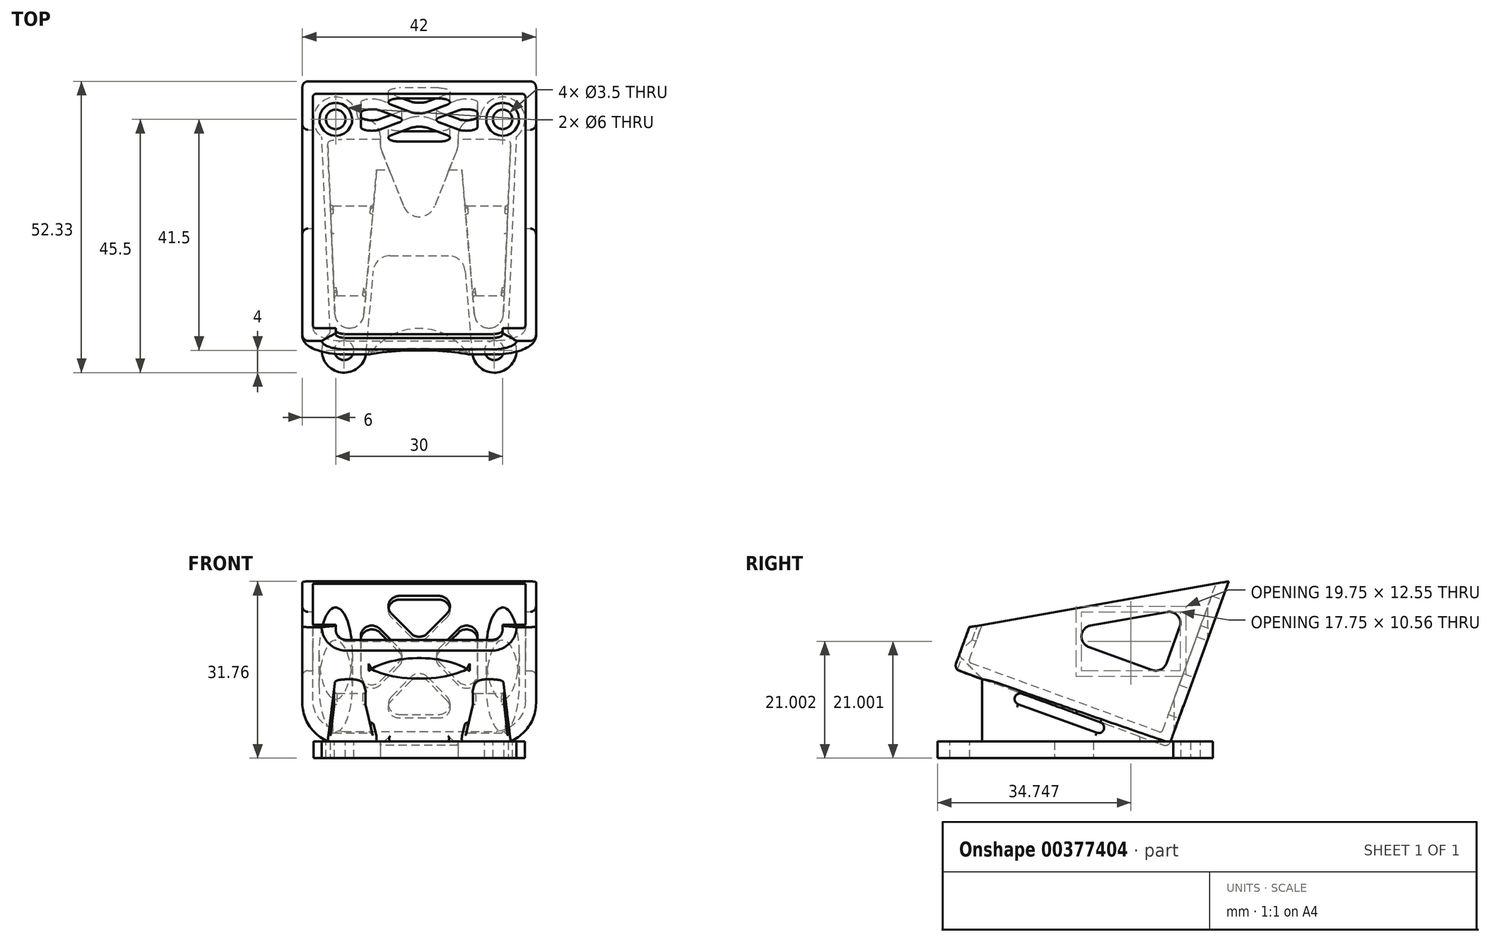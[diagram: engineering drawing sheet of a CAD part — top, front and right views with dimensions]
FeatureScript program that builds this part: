
annotation { "Feature Type Name" : "Feature", "Feature Type Description" : "" }
export const myFeature = defineFeature(function(context is Context, id is Id, definition is map)
    precondition{}
    {
        {
            var Q0;
            Q0=qCreatedBy(makeId("Right.planeOp"),FACE);
            var sketch = newSketch(context, id + "F0", { "sketchPlane" : qUnion([Q0])});
            skLineSegment(sketch, "E0.bottom", {"start": v(-38.53, 14.02) * mm, "end": v(0, 0) * mm});
            skLineSegment(sketch, "E0.top", {"start": v(-24.16, 53.49) * mm, "end": v(14.36, 39.47) * mm});
            skLineSegment(sketch, "E0.left", {"start": v(-38.53, 14.02) * mm, "end": v(-24.16, 53.49) * mm});
            skLineSegment(sketch, "E0.right", {"start": v(0, 0) * mm, "end": v(14.36, 39.47) * mm});
            skPoint(sketch, "E0.middle", {"position": v(-12.08, 26.74) * mm});
            skSolve(sketch);
        }
        {
            var Q0;
            Q0=makeQuery(id+"F0.imprint","IMPRINT",FACE,{"disambiguationData":[TD([[makeQuery(id+"F0.imprint","IMPRINT",EDGE,{"derivedFrom":sQuery(id+"F0.wireOp",EDGE,"E0.bottom")}),1.0]])]});
            extrude(context, id + "F1", {"entities" : qUnion([Q0]), "endBound" : BoundingType.SYMMETRIC, "depth" : 42 * mm});
        }
        {
            var Q0;
            Q0=qCreatedBy(makeId("Right.planeOp"),FACE);
            var sketch = newSketch(context, id + "F2", { "sketchPlane" : qUnion([Q0])});
            skLineSegment(sketch, "E1.bottom", {"start": v(-1.2, 2.56) * mm, "end": v(-35.96, 15.22) * mm});
            skLineSegment(sketch, "E1.top", {"start": v(11.8, 38.27) * mm, "end": v(-22.97, 50.93) * mm});
            skLineSegment(sketch, "E1.left", {"start": v(-1.2, 2.56) * mm, "end": v(11.8, 38.27) * mm});
            skLineSegment(sketch, "E1.right", {"start": v(-35.96, 15.22) * mm, "end": v(-22.97, 50.93) * mm});
            skPoint(sketch, "E1.middle", {"position": v(-12.08, 26.74) * mm});
            skSolve(sketch);
        }
        {
            var Q0;
            Q0=qSketchRegion(id+"F2",true);
            extrude(context, id + "F3", {"entities" : qUnion([Q0]), "operationType" : NewBodyOperationType.REMOVE, "endBound" : BoundingType.SYMMETRIC, "depth" : 38.2 * mm});
        }
        {
            var Q0;
            Q0=makeQuery(id+"F3.boolean.opBoolean","COPY",EDGE,{"derivedFrom":makeQuery(id+"F3.opExtrude","CAP_EDGE",EDGE,{"disambiguationData":[OSD([sQuery(id+"F2.wireOp",EDGE,"E1.top")])],"isStart":false})});
            var Q1;
            Q1=makeQuery(id+"F3.boolean.opBoolean","COPY",EDGE,{"derivedFrom":makeQuery(id+"F3.opExtrude","CAP_EDGE",EDGE,{"disambiguationData":[OSD([sQuery(id+"F2.wireOp",EDGE,"E1.bottom")])],"isStart":false})});
            var Q2;
            Q2=makeQuery(id+"F3.boolean.opBoolean","COPY",EDGE,{"derivedFrom":makeQuery(id+"F3.opExtrude","CAP_EDGE",EDGE,{"disambiguationData":[OSD([sQuery(id+"F2.wireOp",EDGE,"E1.bottom")])],"isStart":true})});
            var Q3;
            Q3=makeQuery(id+"F3.boolean.opBoolean","COPY",EDGE,{"derivedFrom":makeQuery(id+"F3.opExtrude","CAP_EDGE",EDGE,{"disambiguationData":[OSD([sQuery(id+"F2.wireOp",EDGE,"E1.top")])],"isStart":true})});
            fillet(context, id + "F4", {"entities" : qUnion([Q0, Q1, Q2, Q3]), "radius" : 6 * mm, "tangentPropagation" : true, "allowEdgeOverflow" : false});
        }
        {
            var Q0;
            Q0=makeQuery(id+"F1.opExtrude","CAP_EDGE",EDGE,{"disambiguationData":[OSD([sQuery(id+"F0.wireOp",EDGE,"E0.top")])],"isStart":false});
            var Q1;
            Q1=makeQuery(id+"F1.opExtrude","CAP_EDGE",EDGE,{"disambiguationData":[OSD([sQuery(id+"F0.wireOp",EDGE,"E0.top")])],"isStart":true});
            var Q2;
            Q2=makeQuery(id+"F1.opExtrude","CAP_EDGE",EDGE,{"disambiguationData":[OSD([sQuery(id+"F0.wireOp",EDGE,"E0.bottom")])],"isStart":true});
            var Q3;
            Q3=makeQuery(id+"F1.opExtrude","CAP_EDGE",EDGE,{"disambiguationData":[OSD([sQuery(id+"F0.wireOp",EDGE,"E0.bottom")])],"isStart":false});
            fillet(context, id + "F5", {"entities" : qUnion([Q0, Q1, Q2, Q3]), "radius" : 8 * mm, "tangentPropagation" : true, "allowEdgeOverflow" : false});
        }
        {
            var Q0;
            Q0=makeQuery(id+"F1.opExtrude","SWEPT_FACE",FACE,{"disambiguationData":[OSD([sQuery(id+"F0.wireOp",EDGE,"E0.left")])]});
            var sketch = newSketch(context, id + "F6", { "sketchPlane" : qUnion([Q0])});
            skLineSegment(sketch, "E2.bottom", {"start": v(-15, 36) * mm, "end": v(15, 36) * mm});
            skLineSegment(sketch, "E2.top", {"start": v(-15, 6) * mm, "end": v(15, 6) * mm});
            skLineSegment(sketch, "E2.left", {"start": v(-15, 36) * mm, "end": v(-15, 6) * mm});
            skLineSegment(sketch, "E2.right", {"start": v(15, 36) * mm, "end": v(15, 6) * mm});
            skSolve(sketch);
        }
        {
            var Q0;
            Q0=makeQuery(id+"F6.imprint","IMPRINT",FACE,{"disambiguationData":[TD([[makeQuery(id+"F6.imprint","IMPRINT",EDGE,{"derivedFrom":sQuery(id+"F6.wireOp",EDGE,"E2.bottom")}),-1.0]])]});
            extrude(context, id + "F7", {"entities" : qUnion([Q0]), "operationType" : NewBodyOperationType.REMOVE, "oppositeDirection" : true, "depth" : 25 * mm});
        }
        {
            var Q0;
            Q0=makeQuery(id+"F7.boolean.opBoolean","COPY",EDGE,{"derivedFrom":makeQuery(id+"F7.opExtrude","SWEPT_EDGE",EDGE,{"disambiguationData":[OSD([sQuery(id+"F6.wireOp",EDGE,"E2.top"),sQuery(id+"F6.wireOp",EDGE,"E2.left")])]})});
            var Q1;
            Q1=makeQuery(id+"F7.boolean.opBoolean","COPY",EDGE,{"derivedFrom":makeQuery(id+"F7.opExtrude","SWEPT_EDGE",EDGE,{"disambiguationData":[OSD([sQuery(id+"F6.wireOp",EDGE,"E2.top"),sQuery(id+"F6.wireOp",EDGE,"E2.right")])]})});
            var Q2;
            Q2=makeQuery(id+"F7.boolean.opBoolean","COPY",EDGE,{"derivedFrom":makeQuery(id+"F7.opExtrude","SWEPT_EDGE",EDGE,{"disambiguationData":[OSD([sQuery(id+"F6.wireOp",EDGE,"E2.bottom"),sQuery(id+"F6.wireOp",EDGE,"E2.right")])]})});
            var Q3;
            Q3=makeQuery(id+"F7.boolean.opBoolean","COPY",EDGE,{"derivedFrom":makeQuery(id+"F7.opExtrude","SWEPT_EDGE",EDGE,{"disambiguationData":[OSD([sQuery(id+"F6.wireOp",EDGE,"E2.bottom"),sQuery(id+"F6.wireOp",EDGE,"E2.left")])]})});
            fillet(context, id + "F8", {"entities" : qUnion([Q0, Q1, Q2, Q3]), "radius" : 2 * mm, "tangentPropagation" : true, "allowEdgeOverflow" : false});
        }
        {
            var Q0;
            Q0=qCreatedBy(makeId("Right.planeOp"),FACE);
            var sketch = newSketch(context, id + "F9", { "sketchPlane" : qUnion([Q0])});
            skLineSegment(sketch, "E3", {"start": v(-35.8, 21.54) * mm, "end": v(10.83, 29.76) * mm});
            skLineSegment(sketch, "E4", {"start": v(-35.8, 21.54) * mm, "end": v(-24.16, 53.49) * mm});
            skLineSegment(sketch, "E5", {"start": v(-24.16, 53.49) * mm, "end": v(14.36, 39.47) * mm});
            skLineSegment(sketch, "E6", {"start": v(14.36, 39.47) * mm, "end": v(10.83, 29.76) * mm});
            skSolve(sketch);
        }
        {
            var Q0;
            Q0=qSketchRegion(id+"F9",true);
            extrude(context, id + "F10", {"entities" : qUnion([Q0]), "operationType" : NewBodyOperationType.REMOVE, "endBound" : BoundingType.SYMMETRIC, "oppositeDirection" : true, "depth" : 50 * mm});
        }
        {
            var Q0;
            Q0=makeQuery(id+"F8.opFillet","BLEND_EDGE",EDGE,{"blendedFrom":[makeQuery(id+"F7.boolean.opBoolean","COPY",EDGE,{"derivedFrom":makeQuery(id+"F7.opExtrude","SWEPT_EDGE",EDGE,{"disambiguationData":[OSD([sQuery(id+"F6.wireOp",EDGE,"E2.top"),sQuery(id+"F6.wireOp",EDGE,"E2.left")])]})}),makeQuery(id+"F1.opExtrude","SWEPT_FACE",FACE,{"disambiguationData":[OSD([sQuery(id+"F0.wireOp",EDGE,"E0.left")])]})],"blendedInto":[makeQuery(id+"F1.opExtrude","SWEPT_FACE",FACE,{"disambiguationData":[OSD([sQuery(id+"F0.wireOp",EDGE,"E0.left")])]})]});
            chamfer(context, id + "F11", {"entities" : qUnion([Q0]), "chamferType" : ChamferType.TWO_OFFSETS, "width1" : 2.5 * mm, "oppositeDirection" : false, "width2" : 1.25 * mm, "tangentPropagation" : true});
        }
        {
            var Q0;
            Q0=makeQuery(id+"F1.opExtrude","CAP_EDGE",EDGE,{"disambiguationData":[OSD([sQuery(id+"F0.wireOp",EDGE,"E0.right")])],"isStart":false});
            var Q1;
            Q1=makeQuery(id+"F5.opFillet","BLEND_EDGE",EDGE,{"blendedFrom":[makeQuery(id+"F1.opExtrude","CAP_EDGE",EDGE,{"disambiguationData":[OSD([sQuery(id+"F0.wireOp",EDGE,"E0.bottom")])],"isStart":false}),makeQuery(id+"F1.opExtrude","SWEPT_FACE",FACE,{"disambiguationData":[OSD([sQuery(id+"F0.wireOp",EDGE,"E0.left")])]})],"blendedInto":[makeQuery(id+"F1.opExtrude","SWEPT_FACE",FACE,{"disambiguationData":[OSD([sQuery(id+"F0.wireOp",EDGE,"E0.left")])]})]});
            fillet(context, id + "F12", {"entities" : qUnion([Q0, Q1]), "radius" : 1 * mm, "tangentPropagation" : true, "allowEdgeOverflow" : false});
        }
        {
            var Q0;
            Q0=qCreatedBy(makeId("Top.planeOp"),FACE);
            var sketch = newSketch(context, id + "F13", { "sketchPlane" : qUnion([Q0])});
            skCircle(sketch, "E7", {"center": v(-13.5, -37.5) * mm, "radius": 1.75 * mm, "construction": true});
            skCircle(sketch, "E8", {"center": v(-15, 4) * mm, "radius": 1.75 * mm, "construction": true});
            skCircle(sketch, "E9.MirrorC", {"center": v(15, 4) * mm, "radius": 1.75 * mm, "construction": true});
            skCircle(sketch, "E10.MirrorC", {"center": v(13.5, -37.5) * mm, "radius": 1.75 * mm, "construction": true});
            skArc(sketch, "E11", {"start": v(-16, -34.38) * mm, "mid": v(-15.39, -41.03) * mm, "end": v(-9.52, -37.85) * mm});
            skArc(sketch, "E12", {"start": v(9.52, -37.85) * mm, "mid": v(15.39, -41.03) * mm, "end": v(16, -34.38) * mm});
            skArc(sketch, "E13", {"start": v(-11, 4) * mm, "mid": v(-16.73, 7.6) * mm, "end": v(-17.5, 0.88) * mm});
            skArc(sketch, "E14", {"start": v(17.5, 0.88) * mm, "mid": v(16.73, 7.6) * mm, "end": v(11, 4) * mm});
            skLineSegment(sketch, "E15", {"start": v(-9.52, -37.85) * mm, "end": v(-8.24, -23.24) * mm});
            skLineSegment(sketch, "E16", {"start": v(-5.25, -20.5) * mm, "end": v(5.25, -20.5) * mm});
            skLineSegment(sketch, "E17", {"start": v(8.24, -23.24) * mm, "end": v(9.52, -37.85) * mm});
            skPoint(sketch, "E18.visualSharp", {"position": v(-8, -20.5) * mm});
            skArc(sketch, "E18.filletArc", {"start": v(-5.25, -20.5) * mm, "mid": v(-7.28, -21.29) * mm, "end": v(-8.24, -23.24) * mm});
            skPoint(sketch, "E19.visualSharp", {"position": v(8, -20.5) * mm});
            skArc(sketch, "E19.filletArc", {"start": v(8.24, -23.24) * mm, "mid": v(7.28, -21.29) * mm, "end": v(5.25, -20.5) * mm});
            skLineSegment(sketch, "E20", {"start": v(-16, -34.38) * mm, "end": v(-17.5, 0.88) * mm});
            skLineSegment(sketch, "E21.MirrorCS", {"start": v(16, -34.38) * mm, "end": v(17.5, 0.88) * mm});
            skLineSegment(sketch, "E22", {"start": v(-11, 4) * mm, "end": v(-7, 4) * mm});
            skLineSegment(sketch, "E23", {"start": v(-7, 4) * mm, "end": v(-7, -0.43) * mm});
            skLineSegment(sketch, "E24", {"start": v(-6.79, -1.53) * mm, "end": v(-2.79, -11.6) * mm});
            skLineSegment(sketch, "E25.MirrorCS", {"start": v(7, 4) * mm, "end": v(7, -0.43) * mm});
            skLineSegment(sketch, "E26.MirrorCS", {"start": v(6.79, -1.53) * mm, "end": v(2.79, -11.6) * mm});
            skPoint(sketch, "E27.visualSharp", {"position": v(0, -18.63) * mm});
            skArc(sketch, "E27.filletArc", {"start": v(-2.79, -11.6) * mm, "mid": v(0, -13.5) * mm, "end": v(2.79, -11.6) * mm});
            skPoint(sketch, "E28.visualSharp", {"position": v(-7, -1) * mm});
            skArc(sketch, "E28.filletArc", {"start": v(-7, -0.43) * mm, "mid": v(-6.95, -0.99) * mm, "end": v(-6.79, -1.53) * mm});
            skPoint(sketch, "E29.visualSharp", {"position": v(7, -1) * mm});
            skArc(sketch, "E29.filletArc", {"start": v(6.79, -1.53) * mm, "mid": v(6.95, -0.99) * mm, "end": v(7, -0.43) * mm});
            skLineSegment(sketch, "E30.trimOffspring", {"start": v(7, 4) * mm, "end": v(11, 4) * mm});
            skSolve(sketch);
        }
        {
            var Q0;
            Q0=qSketchRegion(id+"F13",true);
            extrude(context, id + "F14", {"entities" : qUnion([Q0]), "operationType" : NewBodyOperationType.ADD, "depth" : 1 * mm, "hasSecondDirection" : true, "secondDirectionOppositeDirection" : true, "secondDirectionDepth" : 2 * mm});
        }
        {
            var Q0;
            {var subQ0=sQuery(id+"F13.wireOp",EDGE,"E16");var subQ2=sQuery(id+"F13.wireOp",EDGE,"E14");var subQ4=sQuery(id+"F13.wireOp",EDGE,"E12");var subQ5=makeQuery(id+"F14.opExtrude","SWEPT_FACE",FACE,{"disambiguationData":[OSD([subQ4])]});var subQ6=sQuery(id+"F0.wireOp",EDGE,"E0.bottom");var subQ9=sQuery(id+"F13.wireOp",EDGE,"E17");var subQ11=sQuery(id+"F13.wireOp",EDGE,"E19.filletArc");var subQ13=sQuery(id+"F13.wireOp",EDGE,"E21.MirrorCS");var subQ15=sQuery(id+"F13.wireOp",EDGE,"E15");var subQ16=sQuery(id+"F13.wireOp",EDGE,"E13");var subQ17=sQuery(id+"F13.wireOp",EDGE,"E11");var subQ18=sQuery(id+"F13.wireOp",EDGE,"E18.filletArc");var subQ19=sQuery(id+"F13.wireOp",EDGE,"E20");Q0=makeQuery(id+"FU2tXwDnlWeOjY7_1.boolean.opBoolean","SPLIT",FACE,{"disambiguationData":[TD([subQ5])],"derivedFrom":makeQuery(id+"F14.boolean.opBoolean","SPLIT",FACE,{"disambiguationData":[TD([makeQuery(id+"F1.opExtrude","SWEPT_FACE",FACE,{"disambiguationData":[OSD([subQ6])]})])],"derivedFrom":makeQuery(id+"F14.opExtrude","CAP_FACE",FACE,{"disambiguationData":[OSD([subQ17,subQ4,subQ16,subQ2,subQ15,subQ0,subQ9,subQ18,subQ11,subQ19,subQ13,sQuery(id+"F13.wireOp",EDGE,"LFwfzHnZ-pg1Y-ZXRW-QcZN-Bii3daT9BQZJ")])],"isStart":false})})});}
            var sketch = newSketch(context, id + "F15", { "sketchPlane" : qUnion([Q0])});
            skCircle(sketch, "E31", {"center": v(15, 4) * mm, "radius": 1.75 * mm});
            skCircle(sketch, "E32.MirrorC", {"center": v(-15, 4) * mm, "radius": 1.75 * mm});
            skSolve(sketch);
        }
        {
            var Q0;
            Q0=qSketchRegion(id+"F15",true);
            extrude(context, id + "F16", {"entities" : qUnion([Q0]), "operationType" : NewBodyOperationType.REMOVE, "depth" : 30 * mm});
        }
        {
            var Q0;
            Q0=qSketchRegion(id+"F15",true);
            extrude(context, id + "F17", {"entities" : qUnion([Q0]), "operationType" : NewBodyOperationType.REMOVE, "oppositeDirection" : true, "depth" : 1 * mm});
        }
        {
            var Q0;
            {var subQ0=sQuery(id+"F13.wireOp",EDGE,"E15");var subQ1=sQuery(id+"F13.wireOp",EDGE,"E13");var subQ2=sQuery(id+"F13.wireOp",EDGE,"E11");var subQ3=sQuery(id+"F13.wireOp",EDGE,"E20");var subQ6=sQuery(id+"F13.wireOp",EDGE,"E16");var subQ7=sQuery(id+"F13.wireOp",EDGE,"E18.filletArc");Q0=makeQuery(id+"F16.boolean.opBoolean","MERGE",FACE,{"derivedFrom":[makeQuery(id+"FU2tXwDnlWeOjY7_1.boolean.opBoolean","SPLIT",FACE,{"disambiguationData":[TD([makeQuery(id+"F14.opExtrude","SWEPT_FACE",FACE,{"disambiguationData":[OSD([subQ2])]})])],"derivedFrom":makeQuery(id+"F14.opExtrude","CAP_FACE",FACE,{"disambiguationData":[OSD([subQ2,sQuery(id+"F13.wireOp",EDGE,"E12"),subQ1,sQuery(id+"F13.wireOp",EDGE,"E14"),subQ0,subQ6,sQuery(id+"F13.wireOp",EDGE,"E17"),subQ7,sQuery(id+"F13.wireOp",EDGE,"E19.filletArc"),subQ3,sQuery(id+"F13.wireOp",EDGE,"E21.MirrorCS"),sQuery(id+"F13.wireOp",EDGE,"LFwfzHnZ-pg1Y-ZXRW-QcZN-Bii3daT9BQZJ")])],"isStart":false})}),makeQuery(id+"F16.opExtrude","CAP_FACE",FACE,{"disambiguationData":[OSD([sQuery(id+"F15.wireOp",EDGE,"E32.MirrorC")])],"isStart":true})]});}
            var sketch = newSketch(context, id + "F18", { "sketchPlane" : qUnion([Q0])});
            skCircle(sketch, "E33", {"center": v(-13.5, -37.5) * mm, "radius": 1.75 * mm});
            skCircle(sketch, "E34", {"center": v(-15, 4) * mm, "radius": 1.75 * mm});
            skCircle(sketch, "E35.MirrorC", {"center": v(13.5, -37.5) * mm, "radius": 1.75 * mm});
            skCircle(sketch, "E36.MirrorC", {"center": v(15, 4) * mm, "radius": 1.75 * mm});
            skSolve(sketch);
        }
        {
            var Q0;
            Q0=qSketchRegion(id+"F18",true);
            extrude(context, id + "F19", {"entities" : qUnion([Q0]), "operationType" : NewBodyOperationType.REMOVE, "oppositeDirection" : true, "depth" : 25 * mm});
        }
        {
            var Q0;
            Q0=makeQuery(id+"F14.opExtrude","CAP_FACE",FACE,{"disambiguationData":[OSD([sQuery(id+"F13.wireOp",EDGE,"E11"),sQuery(id+"F13.wireOp",EDGE,"E12"),sQuery(id+"F13.wireOp",EDGE,"E13"),sQuery(id+"F13.wireOp",EDGE,"E14"),sQuery(id+"F13.wireOp",EDGE,"E15"),sQuery(id+"F13.wireOp",EDGE,"E16"),sQuery(id+"F13.wireOp",EDGE,"E17"),sQuery(id+"F13.wireOp",EDGE,"E18.filletArc"),sQuery(id+"F13.wireOp",EDGE,"E19.filletArc"),sQuery(id+"F13.wireOp",EDGE,"E20"),sQuery(id+"F13.wireOp",EDGE,"E21.MirrorCS"),sQuery(id+"F13.wireOp",EDGE,"E22"),sQuery(id+"F13.wireOp",EDGE,"E23"),sQuery(id+"F13.wireOp",EDGE,"E24"),sQuery(id+"F13.wireOp",EDGE,"E25.MirrorCS"),sQuery(id+"F13.wireOp",EDGE,"E26.MirrorCS"),sQuery(id+"F13.wireOp",EDGE,"E27.filletArc"),sQuery(id+"F13.wireOp",EDGE,"E28.filletArc"),sQuery(id+"F13.wireOp",EDGE,"E29.filletArc"),sQuery(id+"F13.wireOp",EDGE,"E30.trimOffspring")])],"isStart":false});
            var sketch = newSketch(context, id + "F20", { "sketchPlane" : qUnion([Q0])});
            skLineSegment(sketch, "E37", {"start": v(-15.04, -33.5) * mm, "end": v(-16.44, -0.47) * mm});
            skLineSegment(sketch, "E38", {"start": v(-10.14, -33.5) * mm, "end": v(-7.45, -2.75) * mm});
            skLineSegment(sketch, "E39", {"start": v(-16.44, -0.47) * mm, "end": v(-7.45, -0.47) * mm});
            skLineSegment(sketch, "E40", {"start": v(-7.45, -0.47) * mm, "end": v(-7.45, -2.75) * mm});
            skLineSegment(sketch, "E41.MirrorCS", {"start": v(7.45, -0.47) * mm, "end": v(7.45, -2.75) * mm});
            skLineSegment(sketch, "E42.MirrorCS", {"start": v(10.14, -33.5) * mm, "end": v(7.45, -2.75) * mm});
            skLineSegment(sketch, "E43.MirrorCS", {"start": v(15.04, -33.5) * mm, "end": v(16.44, -0.47) * mm});
            skLineSegment(sketch, "E44.MirrorCS", {"start": v(16.44, -0.47) * mm, "end": v(7.45, -0.47) * mm});
            skPoint(sketch, "E45.orphan", {"position": v(-10.05, -32.46) * mm});
            skPoint(sketch, "E46.orphan", {"position": v(10.05, -32.46) * mm});
            skLineSegment(sketch, "E47", {"start": v(-15.04, -33.5) * mm, "end": v(-10.14, -33.5) * mm});
            skPoint(sketch, "E48.center.orphan", {"position": v(-13.5, -37.5) * mm});
            skLineSegment(sketch, "E49.MirrorCS", {"start": v(15.04, -33.5) * mm, "end": v(10.14, -33.5) * mm});
            skSolve(sketch);
        }
        {
            var Q0;
            Q0=qSketchRegion(id+"F20",true);
            extrude(context, id + "F21", {"entities" : qUnion([Q0]), "operationType" : NewBodyOperationType.ADD, "depth" : 17 * mm});
        }
        {
            var Q0;
            Q0=makeQuery(id+"F3.boolean.opBoolean","COPY",FACE,{"derivedFrom":makeQuery(id+"F3.opExtrude","SWEPT_FACE",FACE,{"disambiguationData":[OSD([sQuery(id+"F2.wireOp",EDGE,"E1.left")])]})});
            var sketch = newSketch(context, id + "F22", { "sketchPlane" : qUnion([Q0])});
            skLineSegment(sketch, "E50.bottom", {"start": v(-19.1, 28.52) * mm, "end": v(19.1, 28.52) * mm});
            skLineSegment(sketch, "E50.top", {"start": v(-13.1, 2) * mm, "end": v(13.1, 2) * mm});
            skLineSegment(sketch, "E50.left", {"start": v(-19.1, 28.52) * mm, "end": v(-19.1, 8) * mm});
            skLineSegment(sketch, "E50.right", {"start": v(19.1, 28.52) * mm, "end": v(19.1, 8) * mm});
            skPoint(sketch, "E51.visualSharp", {"position": v(-19.1, 2) * mm});
            skArc(sketch, "E51.filletArc", {"start": v(-19.1, 8) * mm, "mid": v(-17.34, 3.76) * mm, "end": v(-13.1, 2) * mm});
            skPoint(sketch, "E52.visualSharp", {"position": v(19.1, 2) * mm});
            skArc(sketch, "E52.filletArc", {"start": v(13.1, 2) * mm, "mid": v(17.34, 3.76) * mm, "end": v(19.1, 8) * mm});
            skSolve(sketch);
        }
        {
            var Q0;
            Q0=qSketchRegion(id+"F22",true);
            extrude(context, id + "F23", {"entities" : qUnion([Q0]), "operationType" : NewBodyOperationType.REMOVE, "depth" : 36 * mm});
        }
        {
            var Q0;
            Q0=makeQuery(id+"F14.opExtrude","SWEPT_EDGE",EDGE,{"disambiguationData":[OSD([sQuery(id+"F13.wireOp",EDGE,"E25.MirrorCS"),sQuery(id+"F13.wireOp",EDGE,"E30.trimOffspring")])]});
            var Q1;
            Q1=makeQuery(id+"F14.opExtrude","SWEPT_EDGE",EDGE,{"disambiguationData":[OSD([sQuery(id+"F13.wireOp",EDGE,"E22"),sQuery(id+"F13.wireOp",EDGE,"E23")])]});
            fillet(context, id + "F24", {"entities" : qUnion([Q0, Q1]), "radius" : 3 * mm, "tangentPropagation" : true, "allowEdgeOverflow" : false});
        }
        {
            var Q0;
            Q0=makeQuery(id+"F14.opExtrude","SWEPT_EDGE",EDGE,{"disambiguationData":[OSD([sQuery(id+"F13.wireOp",EDGE,"E13"),sQuery(id+"F13.wireOp",EDGE,"E22")])]});
            var Q1;
            Q1=makeQuery(id+"F14.opExtrude","SWEPT_EDGE",EDGE,{"disambiguationData":[OSD([sQuery(id+"F13.wireOp",EDGE,"E14"),sQuery(id+"F13.wireOp",EDGE,"E30.trimOffspring")])]});
            var Q2;
            Q2=makeQuery(id+"F14.opExtrude","SWEPT_EDGE",EDGE,{"disambiguationData":[OSD([sQuery(id+"F13.wireOp",EDGE,"E12"),sQuery(id+"F13.wireOp",EDGE,"E21.MirrorCS")])]});
            var Q3;
            Q3=makeQuery(id+"F14.opExtrude","SWEPT_EDGE",EDGE,{"disambiguationData":[OSD([sQuery(id+"F13.wireOp",EDGE,"E11"),sQuery(id+"F13.wireOp",EDGE,"E20")])]});
            fillet(context, id + "F25", {"entities" : qUnion([Q0, Q1, Q2, Q3]), "radius" : 0.5 * mm, "tangentPropagation" : true, "allowEdgeOverflow" : false});
        }
        {
            var Q0;
            Q0=makeQuery(id+"F14.boolean.opBoolean","INTERSECT",EDGE,{"disambiguationData":[OD(0.0)],"derivedFrom":[makeQuery(id+"F1.opExtrude","SWEPT_FACE",FACE,{"disambiguationData":[OSD([sQuery(id+"F0.wireOp",EDGE,"E0.bottom")])]}),makeQuery(id+"F14.opExtrude","CAP_FACE",FACE,{"disambiguationData":[OSD([sQuery(id+"F13.wireOp",EDGE,"E11"),sQuery(id+"F13.wireOp",EDGE,"E12"),sQuery(id+"F13.wireOp",EDGE,"E13"),sQuery(id+"F13.wireOp",EDGE,"E14"),sQuery(id+"F13.wireOp",EDGE,"E15"),sQuery(id+"F13.wireOp",EDGE,"E16"),sQuery(id+"F13.wireOp",EDGE,"E17"),sQuery(id+"F13.wireOp",EDGE,"E18.filletArc"),sQuery(id+"F13.wireOp",EDGE,"E19.filletArc"),sQuery(id+"F13.wireOp",EDGE,"E20"),sQuery(id+"F13.wireOp",EDGE,"E21.MirrorCS"),sQuery(id+"F13.wireOp",EDGE,"E22"),sQuery(id+"F13.wireOp",EDGE,"E23"),sQuery(id+"F13.wireOp",EDGE,"E24"),sQuery(id+"F13.wireOp",EDGE,"E25.MirrorCS"),sQuery(id+"F13.wireOp",EDGE,"E26.MirrorCS"),sQuery(id+"F13.wireOp",EDGE,"E27.filletArc"),sQuery(id+"F13.wireOp",EDGE,"E28.filletArc"),sQuery(id+"F13.wireOp",EDGE,"E29.filletArc"),sQuery(id+"F13.wireOp",EDGE,"E30.trimOffspring")])],"isStart":false})]});
            var Q1;
            Q1=makeQuery(id+"F14.boolean.opBoolean","INTERSECT",EDGE,{"disambiguationData":[OD(1.0)],"derivedFrom":[makeQuery(id+"F1.opExtrude","SWEPT_FACE",FACE,{"disambiguationData":[OSD([sQuery(id+"F0.wireOp",EDGE,"E0.bottom")])]}),makeQuery(id+"F14.opExtrude","CAP_FACE",FACE,{"disambiguationData":[OSD([sQuery(id+"F13.wireOp",EDGE,"E11"),sQuery(id+"F13.wireOp",EDGE,"E12"),sQuery(id+"F13.wireOp",EDGE,"E13"),sQuery(id+"F13.wireOp",EDGE,"E14"),sQuery(id+"F13.wireOp",EDGE,"E15"),sQuery(id+"F13.wireOp",EDGE,"E16"),sQuery(id+"F13.wireOp",EDGE,"E17"),sQuery(id+"F13.wireOp",EDGE,"E18.filletArc"),sQuery(id+"F13.wireOp",EDGE,"E19.filletArc"),sQuery(id+"F13.wireOp",EDGE,"E20"),sQuery(id+"F13.wireOp",EDGE,"E21.MirrorCS"),sQuery(id+"F13.wireOp",EDGE,"E22"),sQuery(id+"F13.wireOp",EDGE,"E23"),sQuery(id+"F13.wireOp",EDGE,"E24"),sQuery(id+"F13.wireOp",EDGE,"E25.MirrorCS"),sQuery(id+"F13.wireOp",EDGE,"E26.MirrorCS"),sQuery(id+"F13.wireOp",EDGE,"E27.filletArc"),sQuery(id+"F13.wireOp",EDGE,"E28.filletArc"),sQuery(id+"F13.wireOp",EDGE,"E29.filletArc"),sQuery(id+"F13.wireOp",EDGE,"E30.trimOffspring")])],"isStart":false})]});
            fillet(context, id + "F26", {"entities" : qUnion([Q0, Q1]), "radius" : 0.5 * mm, "tangentPropagation" : true, "allowEdgeOverflow" : false});
        }
        {
            var Q0;
            Q0=qCreatedBy(makeId("Right.planeOp"),FACE);
            var sketch = newSketch(context, id + "F27", { "sketchPlane" : qUnion([Q0])});
            skLineSegment(sketch, "E53", {"start": v(-13.98, 21.83) * mm, "end": v(-0.22, 24.26) * mm});
            skLineSegment(sketch, "E54", {"start": v(2.01, 21.6) * mm, "end": v(-0.38, 15.04) * mm});
            skLineSegment(sketch, "E55", {"start": v(-2.94, 13.84) * mm, "end": v(-14.32, 17.98) * mm});
            skPoint(sketch, "E56.visualSharp", {"position": v(-21.33, 20.54) * mm});
            skArc(sketch, "E56.filletArc", {"start": v(-13.98, 21.83) * mm, "mid": v(-15.63, 20.04) * mm, "end": v(-14.32, 17.98) * mm});
            skPoint(sketch, "E57.visualSharp", {"position": v(3.2, 24.86) * mm});
            skArc(sketch, "E57.filletArc", {"start": v(2.01, 21.6) * mm, "mid": v(1.66, 23.58) * mm, "end": v(-0.22, 24.26) * mm});
            skPoint(sketch, "E58.visualSharp", {"position": v(-1.06, 13.16) * mm});
            skArc(sketch, "E58.filletArc", {"start": v(-2.94, 13.84) * mm, "mid": v(-1.41, 13.9) * mm, "end": v(-0.38, 15.04) * mm});
            skSolve(sketch);
        }
        {
            var Q0;
            Q0=qSketchRegion(id+"F27",true);
            extrude(context, id + "F28", {"entities" : qUnion([Q0]), "operationType" : NewBodyOperationType.REMOVE, "endBound" : BoundingType.SYMMETRIC, "oppositeDirection" : true, "depth" : 50 * mm});
        }
        {
            var Q0;
            Q0=makeQuery(id+"F1.opExtrude","SWEPT_FACE",FACE,{"disambiguationData":[OSD([sQuery(id+"F0.wireOp",EDGE,"E0.right")])]});
            var sketch = newSketch(context, id + "F29", { "sketchPlane" : qUnion([Q0])});
            skLineSegment(sketch, "E59.bottom", {"start": v(-3.54, 28.17) * mm, "end": v(3.54, 28.17) * mm});
            skLineSegment(sketch, "E59.top", {"start": v(-3.54, 5.5) * mm, "end": v(3.54, 5.5) * mm});
            skLineSegment(sketch, "E59.left", {"start": v(-10.5, 20.5) * mm, "end": v(-10.5, 13.18) * mm});
            skLineSegment(sketch, "E59.right", {"start": v(10.5, 20.5) * mm, "end": v(10.5, 13.18) * mm});
            skLineSegment(sketch, "E60", {"start": v(-5, 24.81) * mm, "end": v(-1.47, 21) * mm});
            skLineSegment(sketch, "E61", {"start": v(-10.5, 28.17) * mm, "end": v(10.5, 5.5) * mm, "construction": true});
            skLineSegment(sketch, "E62", {"start": v(10.5, 28.17) * mm, "end": v(-10.5, 5.5) * mm, "construction": true});
            skLineSegment(sketch, "E63", {"start": v(-7.03, 21.85) * mm, "end": v(-3.64, 18.2) * mm});
            skLineSegment(sketch, "E64", {"start": v(-7.03, 11.82) * mm, "end": v(-3.64, 15.48) * mm});
            skLineSegment(sketch, "E65", {"start": v(-5, 8.86) * mm, "end": v(-1.47, 12.68) * mm});
            skLineSegment(sketch, "E66.trimOffspring", {"start": v(3.64, 15.48) * mm, "end": v(7.03, 11.82) * mm});
            skLineSegment(sketch, "E67.trimOffspring", {"start": v(1.47, 21) * mm, "end": v(5, 24.81) * mm});
            skLineSegment(sketch, "E68.trimOffspring", {"start": v(1.47, 12.68) * mm, "end": v(5, 8.86) * mm});
            skLineSegment(sketch, "E69.trimOffspring", {"start": v(3.64, 18.2) * mm, "end": v(7.03, 21.85) * mm});
            skPoint(sketch, "E70.visualSharp", {"position": v(0, 19.41) * mm});
            skArc(sketch, "E70.filletArc", {"start": v(-1.47, 21) * mm, "mid": v(0, 20.35) * mm, "end": v(1.47, 21) * mm});
            skPoint(sketch, "E71.visualSharp", {"position": v(-10.5, 8.08) * mm});
            skArc(sketch, "E71.filletArc", {"start": v(-10.5, 13.18) * mm, "mid": v(-9.23, 11.32) * mm, "end": v(-7.03, 11.82) * mm});
            skPoint(sketch, "E72.visualSharp", {"position": v(-8.11, 5.5) * mm});
            skArc(sketch, "E72.filletArc", {"start": v(-5, 8.86) * mm, "mid": v(-5.37, 6.7) * mm, "end": v(-3.54, 5.5) * mm});
            skPoint(sketch, "E73.visualSharp", {"position": v(8.11, 5.5) * mm});
            skArc(sketch, "E73.filletArc", {"start": v(3.54, 5.5) * mm, "mid": v(5.37, 6.7) * mm, "end": v(5, 8.86) * mm});
            skPoint(sketch, "E74.visualSharp", {"position": v(0, 14.26) * mm});
            skArc(sketch, "E74.filletArc", {"start": v(1.47, 12.68) * mm, "mid": v(0, 13.32) * mm, "end": v(-1.47, 12.68) * mm});
            skPoint(sketch, "E75.visualSharp", {"position": v(-2.39, 16.84) * mm});
            skArc(sketch, "E75.filletArc", {"start": v(-3.64, 15.48) * mm, "mid": v(-3.11, 16.84) * mm, "end": v(-3.64, 18.2) * mm});
            skPoint(sketch, "E76.visualSharp", {"position": v(-10.5, 25.6) * mm});
            skArc(sketch, "E76.filletArc", {"start": v(-7.03, 21.85) * mm, "mid": v(-9.23, 22.36) * mm, "end": v(-10.5, 20.5) * mm});
            skPoint(sketch, "E77.visualSharp", {"position": v(2.39, 16.84) * mm});
            skArc(sketch, "E77.filletArc", {"start": v(3.64, 18.2) * mm, "mid": v(3.11, 16.84) * mm, "end": v(3.64, 15.48) * mm});
            skPoint(sketch, "E78.visualSharp", {"position": v(10.5, 8.08) * mm});
            skArc(sketch, "E78.filletArc", {"start": v(7.03, 11.82) * mm, "mid": v(9.23, 11.32) * mm, "end": v(10.5, 13.18) * mm});
            skPoint(sketch, "E79.visualSharp", {"position": v(10.5, 25.6) * mm});
            skArc(sketch, "E79.filletArc", {"start": v(10.5, 20.5) * mm, "mid": v(9.23, 22.36) * mm, "end": v(7.03, 21.85) * mm});
            skPoint(sketch, "E80.visualSharp", {"position": v(8.11, 28.17) * mm});
            skArc(sketch, "E80.filletArc", {"start": v(5, 24.81) * mm, "mid": v(5.37, 26.97) * mm, "end": v(3.54, 28.17) * mm});
            skPoint(sketch, "E81.visualSharp", {"position": v(-8.11, 28.17) * mm});
            skArc(sketch, "E81.filletArc", {"start": v(-3.54, 28.17) * mm, "mid": v(-5.37, 26.97) * mm, "end": v(-5, 24.81) * mm});
            skSolve(sketch);
        }
        {
            var Q0;
            Q0=qSketchRegion(id+"F29",true);
            extrude(context, id + "F30", {"entities" : qUnion([Q0]), "operationType" : NewBodyOperationType.REMOVE, "oppositeDirection" : true, "depth" : 25 * mm});
        }
        {
            var Q0;
            Q0=qCreatedBy(makeId("Right.planeOp"),FACE);
            var sketch = newSketch(context, id + "F31", { "sketchPlane" : qUnion([Q0])});
            skLineSegment(sketch, "E82", {"start": v(-26.65, 8.64) * mm, "end": v(-12.56, 3.5) * mm, "construction": true});
            skArc(sketch, "E83.0.startCap", {"start": v(-27, 7.7) * mm, "mid": v(-27.6, 8.98) * mm, "end": v(-26.31, 9.58) * mm});
            skArc(sketch, "E83.0.endCap", {"start": v(-12.22, 4.45) * mm, "mid": v(-11.62, 3.16) * mm, "end": v(-12.9, 2.57) * mm});
            skLineSegment(sketch, "E83.0.left", {"start": v(-26.31, 9.58) * mm, "end": v(-12.22, 4.45) * mm});
            skLineSegment(sketch, "E83.0.right", {"start": v(-27, 7.7) * mm, "end": v(-12.9, 2.57) * mm});
            skSolve(sketch);
        }
        {
            var Q0;
            Q0=qSketchRegion(id+"F31",true);
            extrude(context, id + "F32", {"entities" : qUnion([Q0]), "operationType" : NewBodyOperationType.REMOVE, "endBound" : BoundingType.SYMMETRIC, "oppositeDirection" : true, "depth" : 50 * mm});
        }
        {
            var Q0;
            Q0=makeQuery(id+"F3.boolean.opBoolean","COPY",EDGE,{"derivedFrom":makeQuery(id+"F3.opExtrude","CAP_EDGE",EDGE,{"disambiguationData":[OSD([sQuery(id+"F2.wireOp",EDGE,"E1.left")])],"isStart":true})});
            var Q1;
            Q1=makeQuery(id+"F4.opFillet","BLEND_EDGE",EDGE,{"blendedFrom":[makeQuery(id+"F3.boolean.opBoolean","COPY",EDGE,{"derivedFrom":makeQuery(id+"F3.opExtrude","CAP_EDGE",EDGE,{"disambiguationData":[OSD([sQuery(id+"F2.wireOp",EDGE,"E1.bottom")])],"isStart":true})}),makeQuery(id+"F3.boolean.opBoolean","COPY",FACE,{"derivedFrom":makeQuery(id+"F3.opExtrude","SWEPT_FACE",FACE,{"disambiguationData":[OSD([sQuery(id+"F2.wireOp",EDGE,"E1.right")])]})})],"blendedInto":[makeQuery(id+"F3.boolean.opBoolean","COPY",FACE,{"derivedFrom":makeQuery(id+"F3.opExtrude","SWEPT_FACE",FACE,{"disambiguationData":[OSD([sQuery(id+"F2.wireOp",EDGE,"E1.right")])]})})]});
            fillet(context, id + "F33", {"entities" : qUnion([Q0, Q1]), "radius" : 0.5 * mm, "tangentPropagation" : true, "allowEdgeOverflow" : false});
        }
        {
            var Q0;
            {var subQ1=sQuery(id+"F0.wireOp",EDGE,"E0.bottom");var subQ2=makeQuery(id+"F1.opExtrude","CAP_EDGE",EDGE,{"disambiguationData":[OSD([subQ1])],"isStart":false});Q0=makeQuery(id+"F32.boolean.opBoolean","INTERSECT",EDGE,{"derivedFrom":[makeQuery(id+"F21.boolean.opBoolean","SPLIT",FACE,{"disambiguationData":[TD([makeQuery(id+"F5.opFillet","BLEND_FACE",FACE,{"disambiguationData":[OSD([subQ1]),TDD([subQ2])]})])],"derivedFrom":makeQuery(id+"F21.opExtrude","SWEPT_FACE",FACE,{"disambiguationData":[OSD([sQuery(id+"F20.wireOp",EDGE,"E43.MirrorCS")])]})}),makeQuery(id+"F32.opExtrude","SWEPT_FACE",FACE,{"disambiguationData":[OSD([sQuery(id+"F31.wireOp",EDGE,"E83.0.left")])]})]});}
            var Q1;
            {var subQ1=sQuery(id+"F0.wireOp",EDGE,"E0.bottom");var subQ2=makeQuery(id+"F1.opExtrude","CAP_EDGE",EDGE,{"disambiguationData":[OSD([subQ1])],"isStart":true});Q1=makeQuery(id+"F32.boolean.opBoolean","INTERSECT",EDGE,{"derivedFrom":[makeQuery(id+"F21.boolean.opBoolean","SPLIT",FACE,{"disambiguationData":[TD([makeQuery(id+"F5.opFillet","BLEND_FACE",FACE,{"disambiguationData":[OSD([subQ1]),TDD([subQ2])]})])],"derivedFrom":makeQuery(id+"F21.opExtrude","SWEPT_FACE",FACE,{"disambiguationData":[OSD([sQuery(id+"F20.wireOp",EDGE,"E37")])]})}),makeQuery(id+"F32.opExtrude","SWEPT_FACE",FACE,{"disambiguationData":[OSD([sQuery(id+"F31.wireOp",EDGE,"E83.0.left")])]})]});}
            var Q2;
            Q2=makeQuery(id+"F32.boolean.opBoolean","INTERSECT",EDGE,{"derivedFrom":[makeQuery(id+"F21.boolean.opBoolean","SPLIT",FACE,{"disambiguationData":[TD([makeQuery(id+"F1.opExtrude","SWEPT_FACE",FACE,{"disambiguationData":[OSD([sQuery(id+"F0.wireOp",EDGE,"E0.bottom")])]})])],"derivedFrom":makeQuery(id+"F21.opExtrude","SWEPT_FACE",FACE,{"disambiguationData":[OSD([sQuery(id+"F20.wireOp",EDGE,"E38")])]})}),makeQuery(id+"F32.opExtrude","SWEPT_FACE",FACE,{"disambiguationData":[OSD([sQuery(id+"F31.wireOp",EDGE,"E83.0.right")])]})]});
            var Q3;
            Q3=makeQuery(id+"F32.boolean.opBoolean","INTERSECT",EDGE,{"derivedFrom":[makeQuery(id+"F21.boolean.opBoolean","SPLIT",FACE,{"disambiguationData":[TD([makeQuery(id+"F1.opExtrude","SWEPT_FACE",FACE,{"disambiguationData":[OSD([sQuery(id+"F0.wireOp",EDGE,"E0.bottom")])]})])],"derivedFrom":makeQuery(id+"F21.opExtrude","SWEPT_FACE",FACE,{"disambiguationData":[OSD([sQuery(id+"F20.wireOp",EDGE,"E42.MirrorCS")])]})}),makeQuery(id+"F32.opExtrude","SWEPT_FACE",FACE,{"disambiguationData":[OSD([sQuery(id+"F31.wireOp",EDGE,"E83.0.right")])]})]});
            fillet(context, id + "F34", {"entities" : qUnion([Q0, Q1, Q2, Q3]), "radius" : 0.5 * mm, "tangentPropagation" : true, "allowEdgeOverflow" : false});
        }
        {
            var Q0;
            Q0=makeQuery(id+"F14.opExtrude","CAP_FACE",FACE,{"disambiguationData":[OSD([sQuery(id+"F13.wireOp",EDGE,"E11"),sQuery(id+"F13.wireOp",EDGE,"E12"),sQuery(id+"F13.wireOp",EDGE,"E13"),sQuery(id+"F13.wireOp",EDGE,"E14"),sQuery(id+"F13.wireOp",EDGE,"E15"),sQuery(id+"F13.wireOp",EDGE,"E16"),sQuery(id+"F13.wireOp",EDGE,"E17"),sQuery(id+"F13.wireOp",EDGE,"E18.filletArc"),sQuery(id+"F13.wireOp",EDGE,"E19.filletArc"),sQuery(id+"F13.wireOp",EDGE,"E20"),sQuery(id+"F13.wireOp",EDGE,"E21.MirrorCS"),sQuery(id+"F13.wireOp",EDGE,"E22"),sQuery(id+"F13.wireOp",EDGE,"E23"),sQuery(id+"F13.wireOp",EDGE,"E24"),sQuery(id+"F13.wireOp",EDGE,"E25.MirrorCS"),sQuery(id+"F13.wireOp",EDGE,"E26.MirrorCS"),sQuery(id+"F13.wireOp",EDGE,"E27.filletArc"),sQuery(id+"F13.wireOp",EDGE,"E28.filletArc"),sQuery(id+"F13.wireOp",EDGE,"E29.filletArc"),sQuery(id+"F13.wireOp",EDGE,"E30.trimOffspring")])],"isStart":false});
            var sketch = newSketch(context, id + "F35", { "sketchPlane" : qUnion([Q0])});
            skCircle(sketch, "E84", {"center": v(15, 4) * mm, "radius": 3 * mm});
            skCircle(sketch, "E85", {"center": v(-15, 4) * mm, "radius": 3 * mm});
            skSolve(sketch);
        }
        {
            var Q0;
            Q0=qSketchRegion(id+"F35",true);
            extrude(context, id + "F36", {"entities" : qUnion([Q0]), "operationType" : NewBodyOperationType.REMOVE, "depth" : 25 * mm});
        }
        {
            var Q0;
            Q0=qCreatedBy(makeId("Top.planeOp"),FACE);
            var sketch = newSketch(context, id + "F37", { "sketchPlane" : qUnion([Q0])});
            skLineSegment(sketch, "E86", {"start": v(-50, 0) * mm, "end": v(50, 0) * mm, "construction": true});
            skSolve(sketch);
        }
        {
            var Q0;
            Q0=sQuery(id+"F37.wireOp",EDGE,"E86");
            cPlane(context, id + "F38", {"entities" : qUnion([Q0]), "cplaneType" : CPlaneType.LINE_ANGLE, "offset" : 25 * mm, "angle" : 45 * degree, "oppositeDirection" : true, "width" : 150 * mm, "height" : 150 * mm});
        }
        {
            var Q0;
            Q0=qCreatedBy(id+"F38.planeOp",FACE);
            var sketch = newSketch(context, id + "F39", { "sketchPlane" : qUnion([Q0])});
            skEllipse(sketch, "E87", {"center": v(0, -20) * mm, "majorRadius": 11 * mm, "minorRadius": 5 * mm, "majorAxis": v(-1, 0)});
            skSolve(sketch);
        }
        {
            var Q0;
            Q0=makeQuery(id+"F39.imprint","IMPRINT",FACE,{"disambiguationData":[TD([[makeQuery(id+"F39.imprint","IMPRINT",EDGE,{"derivedFrom":sQuery(id+"F39.wireOp",EDGE,"E87")}),1.0]])]});
            extrude(context, id + "F40", {"entities" : qUnion([Q0]), "operationType" : NewBodyOperationType.REMOVE, "oppositeDirection" : true, "depth" : 60 * mm, "hasSecondDirection" : true, "secondDirectionOppositeDirection" : true, "secondDirectionDepth" : 30 * mm});
        }
        {
            var Q0;
            Q0=makeQuery(id+"F40.boolean.opBoolean","INTERSECT",EDGE,{"derivedFrom":[makeQuery(id+"F1.opExtrude","SWEPT_FACE",FACE,{"disambiguationData":[OSD([sQuery(id+"F0.wireOp",EDGE,"E0.left")])]}),makeQuery(id+"F40.opExtrude","SWEPT_FACE",FACE,{"disambiguationData":[OSD([sQuery(id+"F39.wireOp",EDGE,"E87")])]})]});
            fillet(context, id + "F41", {"entities" : qUnion([Q0]), "radius" : 1 * mm, "tangentPropagation" : true, "allowEdgeOverflow" : false});
        }
        {
            var Q0;
            {var subQ0=sQuery(id+"F0.wireOp",EDGE,"E0.bottom");var subQ1=sQuery(id+"F20.wireOp",EDGE,"E47");var subQ2=sQuery(id+"F20.wireOp",EDGE,"E37");Q0=makeQuery(id+"F21.boolean.opBoolean","SPLIT",EDGE,{"disambiguationData":[TD([makeQuery(id+"F5.opFillet","BLEND_FACE",FACE,{"disambiguationData":[OSD([subQ0]),TDD([makeQuery(id+"F1.opExtrude","CAP_EDGE",EDGE,{"disambiguationData":[OSD([subQ0])],"isStart":true})])]})])],"derivedFrom":makeQuery(id+"F21.opExtrude","SWEPT_EDGE",EDGE,{"disambiguationData":[OSD([subQ2,subQ1])]})});}
            var Q1;
            {var subQ0=sQuery(id+"F20.wireOp",EDGE,"E38");var subQ1=sQuery(id+"F20.wireOp",EDGE,"E47");Q1=makeQuery(id+"F21.boolean.opBoolean","SPLIT",EDGE,{"disambiguationData":[TD([makeQuery(id+"F1.opExtrude","SWEPT_FACE",FACE,{"disambiguationData":[OSD([sQuery(id+"F0.wireOp",EDGE,"E0.bottom")])]})])],"derivedFrom":makeQuery(id+"F21.opExtrude","SWEPT_EDGE",EDGE,{"disambiguationData":[OSD([subQ0,subQ1])]})});}
            var Q2;
            {var subQ0=sQuery(id+"F20.wireOp",EDGE,"E49.MirrorCS");var subQ1=sQuery(id+"F20.wireOp",EDGE,"E42.MirrorCS");Q2=makeQuery(id+"F21.boolean.opBoolean","SPLIT",EDGE,{"disambiguationData":[TD([makeQuery(id+"F1.opExtrude","SWEPT_FACE",FACE,{"disambiguationData":[OSD([sQuery(id+"F0.wireOp",EDGE,"E0.bottom")])]})])],"derivedFrom":makeQuery(id+"F21.opExtrude","SWEPT_EDGE",EDGE,{"disambiguationData":[OSD([subQ1,subQ0])]})});}
            var Q3;
            {var subQ0=sQuery(id+"F0.wireOp",EDGE,"E0.bottom");var subQ1=sQuery(id+"F20.wireOp",EDGE,"E49.MirrorCS");var subQ2=sQuery(id+"F20.wireOp",EDGE,"E43.MirrorCS");Q3=makeQuery(id+"F21.boolean.opBoolean","SPLIT",EDGE,{"disambiguationData":[TD([makeQuery(id+"F5.opFillet","BLEND_FACE",FACE,{"disambiguationData":[OSD([subQ0]),TDD([makeQuery(id+"F1.opExtrude","CAP_EDGE",EDGE,{"disambiguationData":[OSD([subQ0])],"isStart":false})])]})])],"derivedFrom":makeQuery(id+"F21.opExtrude","SWEPT_EDGE",EDGE,{"disambiguationData":[OSD([subQ2,subQ1])]})});}
            fillet(context, id + "F42", {"entities" : qUnion([Q0, Q1, Q2, Q3]), "radius" : 2.6 * mm, "tangentPropagation" : true, "allowEdgeOverflow" : false});
        }
        {
            var Q0;
            Q0=makeQuery(id+"F28.boolean.opBoolean","INTERSECT",EDGE,{"derivedFrom":[makeQuery(id+"F1.opExtrude","CAP_FACE",FACE,{"disambiguationData":[OSD([sQuery(id+"F0.wireOp",EDGE,"E0.bottom"),sQuery(id+"F0.wireOp",EDGE,"E0.top"),sQuery(id+"F0.wireOp",EDGE,"E0.left"),sQuery(id+"F0.wireOp",EDGE,"E0.right")])],"isStart":false}),makeQuery(id+"F28.opExtrude","SWEPT_FACE",FACE,{"disambiguationData":[OSD([sQuery(id+"F27.wireOp",EDGE,"E55")])]})]});
            var Q1;
            Q1=makeQuery(id+"F30.boolean.opBoolean","COPY",EDGE,{"derivedFrom":makeQuery(id+"F30.opExtrude","CAP_EDGE",EDGE,{"disambiguationData":[OSD([sQuery(id+"F29.wireOp",EDGE,"E63")])],"isStart":true})});
            var Q2;
            Q2=makeQuery(id+"F30.boolean.opBoolean","COPY",EDGE,{"derivedFrom":makeQuery(id+"F30.opExtrude","CAP_EDGE",EDGE,{"disambiguationData":[OSD([sQuery(id+"F29.wireOp",EDGE,"E60")])],"isStart":true})});
            var Q3;
            Q3=makeQuery(id+"F30.boolean.opBoolean","COPY",EDGE,{"derivedFrom":makeQuery(id+"F30.opExtrude","CAP_EDGE",EDGE,{"disambiguationData":[OSD([sQuery(id+"F29.wireOp",EDGE,"E59.right")])],"isStart":true})});
            var Q4;
            Q4=makeQuery(id+"F30.boolean.opBoolean","COPY",EDGE,{"derivedFrom":makeQuery(id+"F30.opExtrude","CAP_EDGE",EDGE,{"disambiguationData":[OSD([sQuery(id+"F29.wireOp",EDGE,"E68.trimOffspring")])],"isStart":true})});
            var Q5;
            Q5=makeQuery(id+"F28.boolean.opBoolean","INTERSECT",EDGE,{"derivedFrom":[makeQuery(id+"F1.opExtrude","CAP_FACE",FACE,{"disambiguationData":[OSD([sQuery(id+"F0.wireOp",EDGE,"E0.bottom"),sQuery(id+"F0.wireOp",EDGE,"E0.top"),sQuery(id+"F0.wireOp",EDGE,"E0.left"),sQuery(id+"F0.wireOp",EDGE,"E0.right")])],"isStart":true}),makeQuery(id+"F28.opExtrude","SWEPT_FACE",FACE,{"disambiguationData":[OSD([sQuery(id+"F27.wireOp",EDGE,"E55")])]})]});
            fillet(context, id + "F43", {"entities" : qUnion([Q0, Q1, Q2, Q3, Q4, Q5]), "radius" : 1 * mm, "tangentPropagation" : true, "allowEdgeOverflow" : false});
        }
    });
